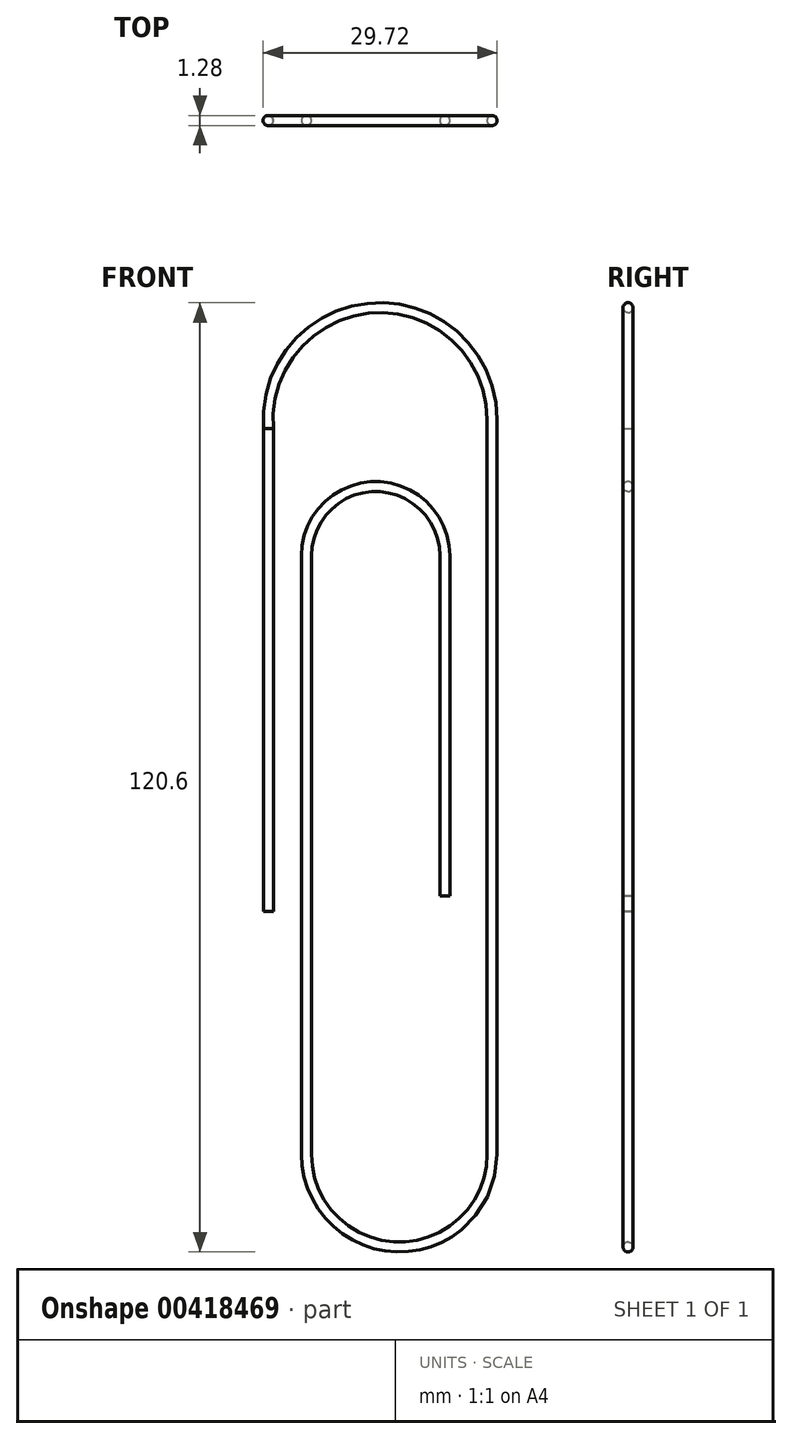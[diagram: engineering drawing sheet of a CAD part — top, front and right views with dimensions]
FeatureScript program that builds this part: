
annotation { "Feature Type Name" : "Feature", "Feature Type Description" : "" }
export const myFeature = defineFeature(function(context is Context, id is Id, definition is map)
    precondition{}
    {
        {
            var Q0;
            Q0=qCreatedBy(makeId("Front.planeOp"),FACE);
            var sketch = newSketch(context, id + "F0", { "sketchPlane" : qUnion([Q0])});
            skLineSegment(sketch, "E0", {"start": v(-33.13, -24.82) * mm, "end": v(-33.13, 36.55) * mm});
            skArc(sketch, "E1", {"start": v(-4.71, 37.68) * mm, "mid": v(-19.5, 51.9) * mm, "end": v(-33.13, 36.55) * mm});
            skLineSegment(sketch, "E2", {"start": v(-4.71, 37.68) * mm, "end": v(-4.71, -55.63) * mm});
            skArc(sketch, "E3", {"start": v(-28.3, -55.63) * mm, "mid": v(-16.5, -67.42) * mm, "end": v(-4.71, -55.63) * mm});
            skLineSegment(sketch, "E4", {"start": v(-28.3, -55.63) * mm, "end": v(-28.3, 20.4) * mm});
            skArc(sketch, "E5", {"start": v(-10.71, 20.4) * mm, "mid": v(-19.5, 29.18) * mm, "end": v(-28.3, 20.4) * mm});
            skLineSegment(sketch, "E6", {"start": v(-10.71, 20.4) * mm, "end": v(-10.71, -22.83) * mm});
            skPoint(sketch, "E7.orphan", {"position": v(-33.13, 37.68) * mm});
            skSolve(sketch);
        }
        {
            var Q0;
            Q0=sQuery(id+"F0.wireOp",VERTEX,"E0.start");
            var Q1;
            Q1=qCreatedBy(makeId("Top.planeOp"),FACE);
            cPlane(context, id + "F1", {"entities" : qUnion([Q0, Q1]), "cplaneType" : CPlaneType.PLANE_POINT, "offset" : 25.4 * mm, "width" : 152.4 * mm, "height" : 152.4 * mm});
        }
        {
            var Q0;
            Q0=qCreatedBy(id+"F1.planeOp",FACE);
            var sketch = newSketch(context, id + "F2", { "sketchPlane" : qUnion([Q0])});
            skCircle(sketch, "E8", {"center": v(-33.13, 0) * mm, "radius": 0.64 * mm});
            skSolve(sketch);
        }
        {
            var Q0;
            Q0 = qSketchRegion(id + "F2", true);
            var Q1;
            Q1=sQuery(id+"F2.wireOp",EDGE,"E8");
            var Q2;
            Q2 = qConstructionFilter(qBodyType(qCreatedBy(id + "F0" ,EDGE), BodyType.WIRE), ConstructionObject.NO);
            sweep(context, id + "F3", {"profiles" : qUnion([Q0]), "surfaceProfiles" : qUnion([Q1]), "path" : qUnion([Q2])});
        }
    });
